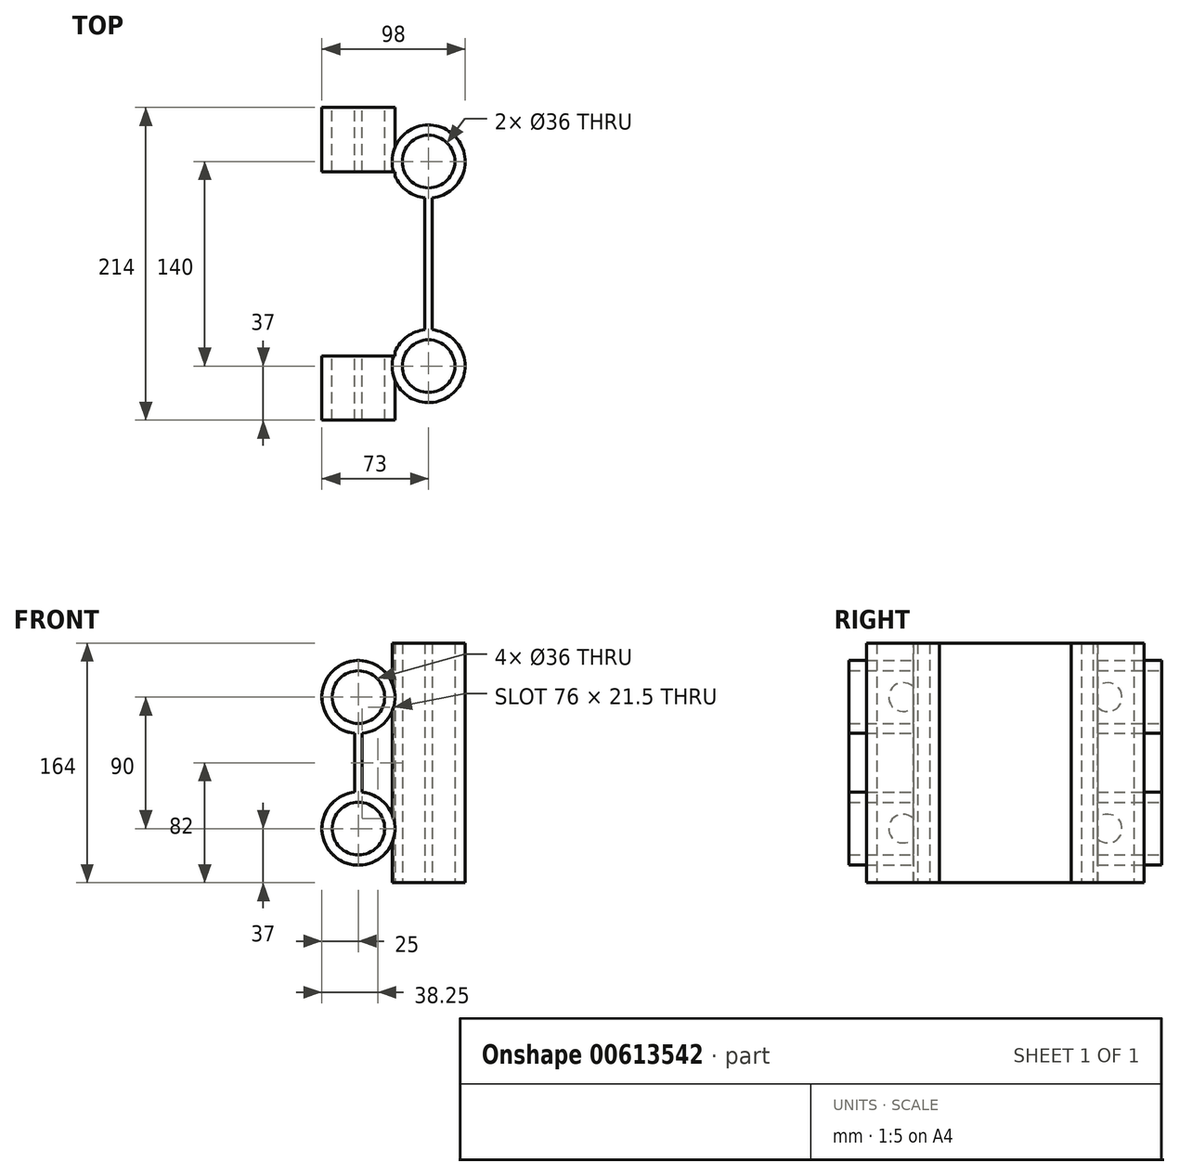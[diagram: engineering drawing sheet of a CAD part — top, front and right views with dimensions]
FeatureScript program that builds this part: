
annotation { "Feature Type Name" : "Feature", "Feature Type Description" : "" }
export const myFeature = defineFeature(function(context is Context, id is Id, definition is map)
    precondition{}
    {
        {
            var Q0;
            Q0=qCreatedBy(makeId("Front.planeOp"),FACE);
            var sketch = newSketch(context, id + "F0", { "sketchPlane" : qUnion([Q0])});
            skCircle(sketch, "E0", {"center": v(-48, 45) * mm, "radius": 18 * mm});
            skCircle(sketch, "E1", {"center": v(-48, -45) * mm, "radius": 18 * mm});
            skCircle(sketch, "E2", {"center": v(-48, 45) * mm, "radius": 25 * mm});
            skCircle(sketch, "E3", {"center": v(-48, -45) * mm, "radius": 25 * mm});
            skLineSegment(sketch, "E4.bottom", {"start": v(-50.5, 20.13) * mm, "end": v(-45.5, 20.13) * mm});
            skLineSegment(sketch, "E4.top", {"start": v(-50.5, -20.13) * mm, "end": v(-45.5, -20.13) * mm});
            skLineSegment(sketch, "E4.left", {"start": v(-50.5, 20.13) * mm, "end": v(-50.5, -20.13) * mm});
            skLineSegment(sketch, "E4.right", {"start": v(-45.5, 20.13) * mm, "end": v(-45.5, -20.13) * mm});
            skLineSegment(sketch, "E5", {"start": v(-48, 20.13) * mm, "end": v(-48, 45) * mm, "construction": true});
            skSolve(sketch);
        }
        {
            var Q0;
            Q0=qCreatedBy(makeId("Top.planeOp"),FACE);
            var sketch = newSketch(context, id + "F1", { "sketchPlane" : qUnion([Q0])});
            skCircle(sketch, "E6", {"center": v(0, 70) * mm, "radius": 18 * mm});
            skCircle(sketch, "E7", {"center": v(0, -70) * mm, "radius": 18 * mm});
            skCircle(sketch, "E8", {"center": v(0, 70) * mm, "radius": 25 * mm});
            skCircle(sketch, "E9", {"center": v(0, -70) * mm, "radius": 25 * mm});
            skLineSegment(sketch, "E10.bottom", {"start": v(-2.5, 45.13) * mm, "end": v(2.5, 45.13) * mm});
            skLineSegment(sketch, "E10.top", {"start": v(-2.5, -45.13) * mm, "end": v(2.5, -45.13) * mm});
            skLineSegment(sketch, "E10.left", {"start": v(-2.5, 45.13) * mm, "end": v(-2.5, -45.13) * mm});
            skLineSegment(sketch, "E10.right", {"start": v(2.5, 45.13) * mm, "end": v(2.5, -45.13) * mm});
            skLineSegment(sketch, "E11", {"start": v(0, 45.13) * mm, "end": v(0, 70) * mm, "construction": true});
            skSolve(sketch);
        }
        {
            var Q0;
            {var subQ0=sQuery(id+"F0.wireOp",EDGE,"E4.left");Q0=makeQuery(id+"F0.imprint","IMPRINT",FACE,{"disambiguationData":[TD([[makeQuery(id+"F0.imprint","IMPRINT",EDGE,{"derivedFrom":subQ0}),1.0]])]});}
            var Q1;
            {var subQ0=sQuery(id+"F0.wireOp",EDGE,"E4.bottom");Q1=makeQuery(id+"F0.imprint","IMPRINT",FACE,{"disambiguationData":[TD([[makeQuery(id+"F0.imprint","IMPRINT",EDGE,{"derivedFrom":subQ0}),-1.0]])]});}
            var Q2;
            {var subQ0=sQuery(id+"F0.wireOp",EDGE,"E4.top");Q2=makeQuery(id+"F0.imprint","IMPRINT",FACE,{"disambiguationData":[TD([[makeQuery(id+"F0.imprint","IMPRINT",EDGE,{"derivedFrom":subQ0}),1.0]])]});}
            extrude(context, id + "F2", {"entities" : qUnion([Q0, Q1, Q2]), "depth" : 107 * mm, "offsetDistance" : 25 * mm, "hasSecondDirection" : true, "secondDirectionOppositeDirection" : true, "secondDirectionDepth" : 107 * mm});
        }
        {
            var Q0;
            Q0=makeQuery(id+"F0.imprint","IMPRINT",FACE,{"disambiguationData":[TD([[makeQuery(id+"F0.imprint","IMPRINT",EDGE,{"derivedFrom":sQuery(id+"F0.wireOp",EDGE,"E0")}),-1.0]])]});
            var Q1;
            Q1=makeQuery(id+"F0.imprint","IMPRINT",FACE,{"disambiguationData":[TD([[makeQuery(id+"F0.imprint","IMPRINT",EDGE,{"derivedFrom":sQuery(id+"F0.wireOp",EDGE,"E1")}),-1.0]])]});
            extrude(context, id + "F3", {"entities" : qUnion([Q0, Q1]), "operationType" : NewBodyOperationType.ADD, "depth" : 107 * mm, "offsetDistance" : 25 * mm, "hasSecondDirection" : true, "secondDirectionOppositeDirection" : true, "secondDirectionDepth" : 107 * mm});
        }
        {
            var Q0;
            Q0=makeQuery(id+"F1.imprint","IMPRINT",FACE,{"disambiguationData":[TD([[makeQuery(id+"F1.imprint","IMPRINT",EDGE,{"derivedFrom":sQuery(id+"F1.wireOp",EDGE,"E6")}),-1.0]])]});
            var Q1;
            {var subQ0=sQuery(id+"F1.wireOp",EDGE,"E10.bottom");Q1=makeQuery(id+"F1.imprint","IMPRINT",FACE,{"disambiguationData":[TD([[makeQuery(id+"F1.imprint","IMPRINT",EDGE,{"derivedFrom":subQ0}),-1.0]])]});}
            var Q2;
            {var subQ0=sQuery(id+"F1.wireOp",EDGE,"E10.left");Q2=makeQuery(id+"F1.imprint","IMPRINT",FACE,{"disambiguationData":[TD([[makeQuery(id+"F1.imprint","IMPRINT",EDGE,{"derivedFrom":subQ0}),1.0]])]});}
            var Q3;
            {var subQ0=sQuery(id+"F1.wireOp",EDGE,"E10.top");Q3=makeQuery(id+"F1.imprint","IMPRINT",FACE,{"disambiguationData":[TD([[makeQuery(id+"F1.imprint","IMPRINT",EDGE,{"derivedFrom":subQ0}),1.0]])]});}
            var Q4;
            Q4=makeQuery(id+"F1.imprint","IMPRINT",FACE,{"disambiguationData":[TD([[makeQuery(id+"F1.imprint","IMPRINT",EDGE,{"derivedFrom":sQuery(id+"F1.wireOp",EDGE,"E7")}),-1.0]])]});
            extrude(context, id + "F4", {"entities" : qUnion([Q0, Q1, Q2, Q3, Q4]), "operationType" : NewBodyOperationType.ADD, "depth" : 82 * mm, "offsetDistance" : 25 * mm, "hasSecondDirection" : true, "secondDirectionOppositeDirection" : true, "secondDirectionDepth" : 82 * mm});
        }
        {
            var Q0;
            Q0=qCreatedBy(makeId("Top.planeOp"),FACE);
            var sketch = newSketch(context, id + "F5", { "sketchPlane" : qUnion([Q0])});
            skLineSegment(sketch, "E12.bottom", {"start": v(-73.05, 63) * mm, "end": v(-22.95, 63) * mm});
            skLineSegment(sketch, "E12.top", {"start": v(-73.05, -63) * mm, "end": v(-22.95, -63) * mm});
            skLineSegment(sketch, "E12.left", {"start": v(-73.05, 63) * mm, "end": v(-73.05, -63) * mm});
            skLineSegment(sketch, "E12.right", {"start": v(-22.95, 63) * mm, "end": v(-22.95, -63) * mm});
            skLineSegment(sketch, "E13", {"start": v(-48, 0) * mm, "end": v(-48, -107) * mm, "construction": true});
            skPoint(sketch, "E13.endSnap0", {"position": v(-48, -63) * mm});
            skSolve(sketch);
        }
        {
            var Q0;
            Q0 = qSketchRegion(id + "F5", true);
            extrude(context, id + "F6", {"entities" : qUnion([Q0]), "operationType" : NewBodyOperationType.REMOVE, "endBound" : BoundingType.THROUGH_ALL, "oppositeDirection" : true, "depth" : 25 * mm, "offsetDistance" : 25 * mm, "hasSecondDirection" : true, "secondDirectionBound" : SecondDirectionBoundingType.THROUGH_ALL, "secondDirectionOppositeDirection" : false, "secondDirectionDepth" : 25 * mm});
        }
    });
